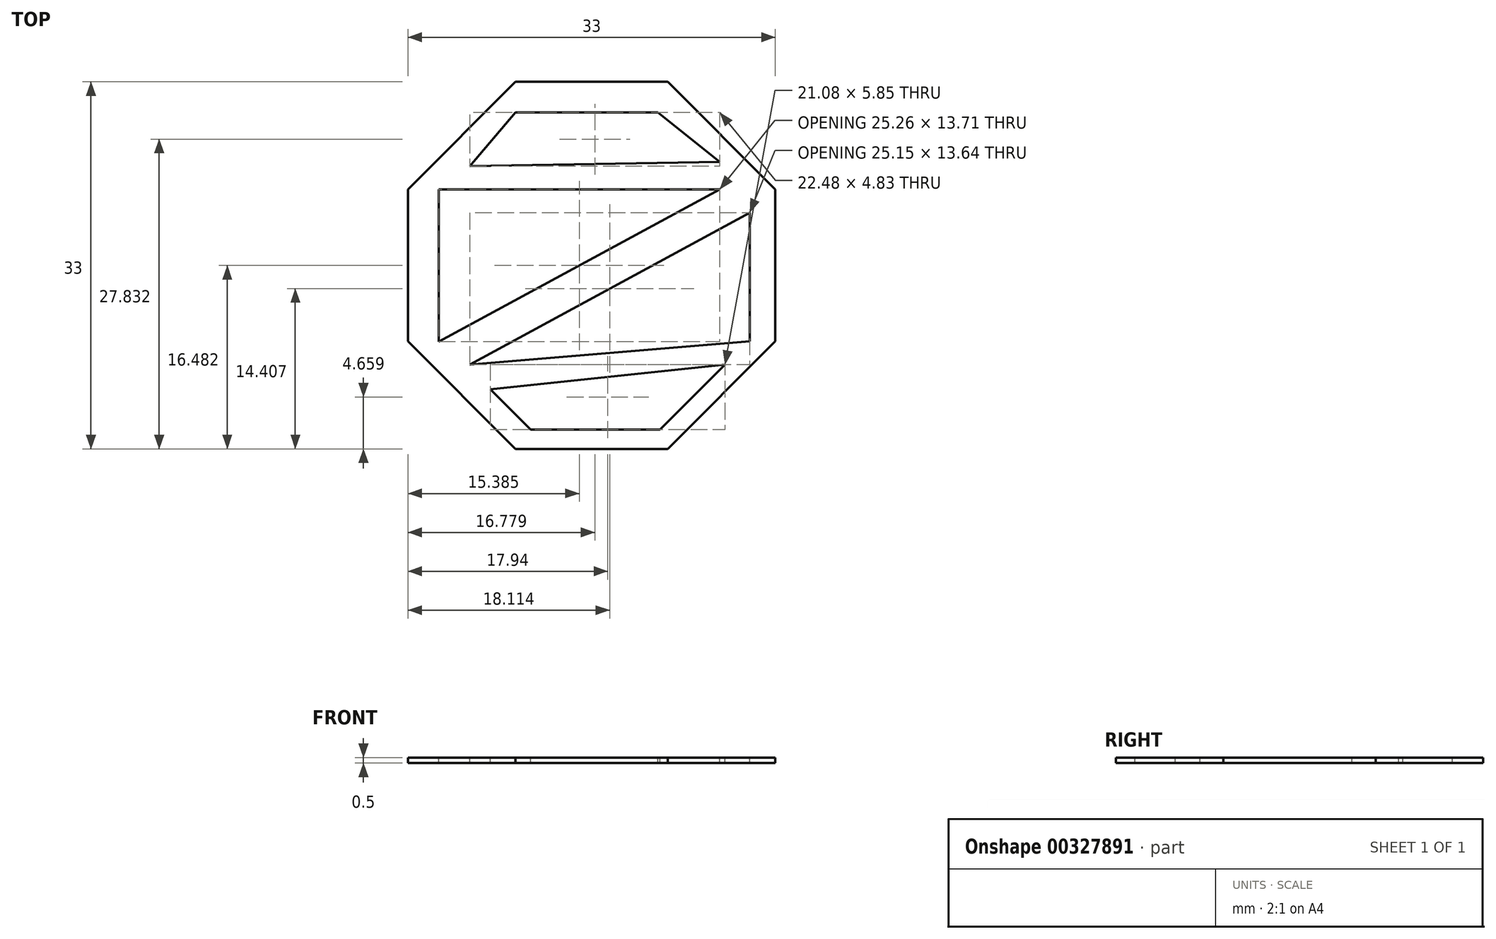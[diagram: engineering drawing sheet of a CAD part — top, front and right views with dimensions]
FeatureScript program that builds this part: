
annotation { "Feature Type Name" : "Feature", "Feature Type Description" : "" }
export const myFeature = defineFeature(function(context is Context, id is Id, definition is map)
    precondition{}
    {
        {
            var Q0;
            Q0=qCreatedBy(makeId("Top.planeOp"),FACE);
            var sketch = newSketch(context, id + "F0", { "sketchPlane" : qUnion([Q0])});
            skCircle(sketch, "E0.cCircle", {"center": v(0, 0) * mm, "radius": 16.5 * mm, "construction": true});
            skLineSegment(sketch, "E0.0", {"start": v(-16.5, -6.83) * mm, "end": v(-16.5, 6.83) * mm});
            skLineSegment(sketch, "E0.1", {"start": v(-16.5, 6.83) * mm, "end": v(-6.83, 16.5) * mm});
            skLineSegment(sketch, "E0.2", {"start": v(-6.83, 16.5) * mm, "end": v(6.83, 16.5) * mm});
            skLineSegment(sketch, "E0.3", {"start": v(6.83, 16.5) * mm, "end": v(16.5, 6.83) * mm});
            skLineSegment(sketch, "E0.4", {"start": v(16.5, 6.83) * mm, "end": v(16.5, -6.83) * mm});
            skLineSegment(sketch, "E0.5", {"start": v(16.5, -6.83) * mm, "end": v(6.83, -16.5) * mm});
            skLineSegment(sketch, "E0.6", {"start": v(6.83, -16.5) * mm, "end": v(-6.83, -16.5) * mm});
            skLineSegment(sketch, "E0.7", {"start": v(-6.83, -16.5) * mm, "end": v(-16.5, -6.83) * mm});
            skPoint(sketch, "E0.0.midPoint", {"position": v(-16.5, 0) * mm});
            skSolve(sketch);
        }
        {
            var Q0;
            Q0=makeQuery(id+"F0.imprint","IMPRINT",FACE,{"disambiguationData":[TD([[makeQuery(id+"F0.imprint","IMPRINT",EDGE,{"derivedFrom":sQuery(id+"F0.wireOp",EDGE,"E0.0")}),-1.0]])]});
            extrude(context, id + "F1", {"entities" : qUnion([Q0]), "depth" : 0.5 * mm});
        }
        {
            var Q0;
            Q0=makeQuery(id+"F1.opExtrude","CAP_FACE",FACE,{"disambiguationData":[OSD([sQuery(id+"F0.wireOp",EDGE,"E0.0"),sQuery(id+"F0.wireOp",EDGE,"E0.1"),sQuery(id+"F0.wireOp",EDGE,"E0.2"),sQuery(id+"F0.wireOp",EDGE,"E0.3"),sQuery(id+"F0.wireOp",EDGE,"E0.4"),sQuery(id+"F0.wireOp",EDGE,"E0.5"),sQuery(id+"F0.wireOp",EDGE,"E0.6"),sQuery(id+"F0.wireOp",EDGE,"E0.7")])],"isStart":false});
            var sketch = newSketch(context, id + "F2", { "sketchPlane" : qUnion([Q0])});
            skLineSegment(sketch, "E1", {"start": v(-13.75, 6.83) * mm, "end": v(-13.75, -6.87) * mm});
            skLineSegment(sketch, "E2", {"start": v(-13.75, -6.87) * mm, "end": v(11.52, 6.83) * mm});
            skLineSegment(sketch, "E3", {"start": v(11.52, 6.83) * mm, "end": v(-13.75, 6.83) * mm});
            skLineSegment(sketch, "E4", {"start": v(-10.96, -8.91) * mm, "end": v(14.19, 4.73) * mm});
            skLineSegment(sketch, "E5", {"start": v(14.19, 4.73) * mm, "end": v(14.19, -6.83) * mm});
            skLineSegment(sketch, "E6", {"start": v(14.19, -6.83) * mm, "end": v(-10.96, -8.91) * mm});
            skLineSegment(sketch, "E7", {"start": v(-10.96, 8.92) * mm, "end": v(-6.83, 13.75) * mm});
            skLineSegment(sketch, "E8", {"start": v(-6.83, 13.75) * mm, "end": v(5.94, 13.75) * mm});
            skLineSegment(sketch, "E9", {"start": v(5.94, 13.75) * mm, "end": v(11.52, 9.29) * mm});
            skLineSegment(sketch, "E10", {"start": v(11.52, 9.29) * mm, "end": v(-10.96, 8.92) * mm});
            skLineSegment(sketch, "E11", {"start": v(-9.1, -11.14) * mm, "end": v(-5.48, -14.77) * mm});
            skLineSegment(sketch, "E12", {"start": v(-5.48, -14.77) * mm, "end": v(6.13, -14.77) * mm});
            skLineSegment(sketch, "E13", {"start": v(6.13, -14.77) * mm, "end": v(11.98, -8.91) * mm});
            skLineSegment(sketch, "E14", {"start": v(11.98, -8.91) * mm, "end": v(-9.1, -11.14) * mm});
            skSolve(sketch);
        }
        {
            var Q0;
            Q0=makeQuery(id+"F2.imprint","IMPRINT",FACE,{"disambiguationData":[TD([[makeQuery(id+"F2.imprint","IMPRINT",EDGE,{"derivedFrom":sQuery(id+"F2.wireOp",EDGE,"E1")}),1.0]])]});
            var Q1;
            Q1=makeQuery(id+"F2.imprint","IMPRINT",FACE,{"disambiguationData":[TD([[makeQuery(id+"F2.imprint","IMPRINT",EDGE,{"derivedFrom":sQuery(id+"F2.wireOp",EDGE,"E7")}),-1.0]])]});
            var Q2;
            Q2=makeQuery(id+"F2.imprint","IMPRINT",FACE,{"disambiguationData":[TD([[makeQuery(id+"F2.imprint","IMPRINT",EDGE,{"derivedFrom":sQuery(id+"F2.wireOp",EDGE,"E4")}),-1.0]])]});
            var Q3;
            Q3=makeQuery(id+"F2.imprint","IMPRINT",FACE,{"disambiguationData":[TD([[makeQuery(id+"F2.imprint","IMPRINT",EDGE,{"derivedFrom":sQuery(id+"F2.wireOp",EDGE,"E11")}),1.0]])]});
            extrude(context, id + "F3", {"entities" : qUnion([Q0, Q1, Q2, Q3]), "operationType" : NewBodyOperationType.REMOVE, "oppositeDirection" : true, "depth" : 1 * mm});
        }
    });
